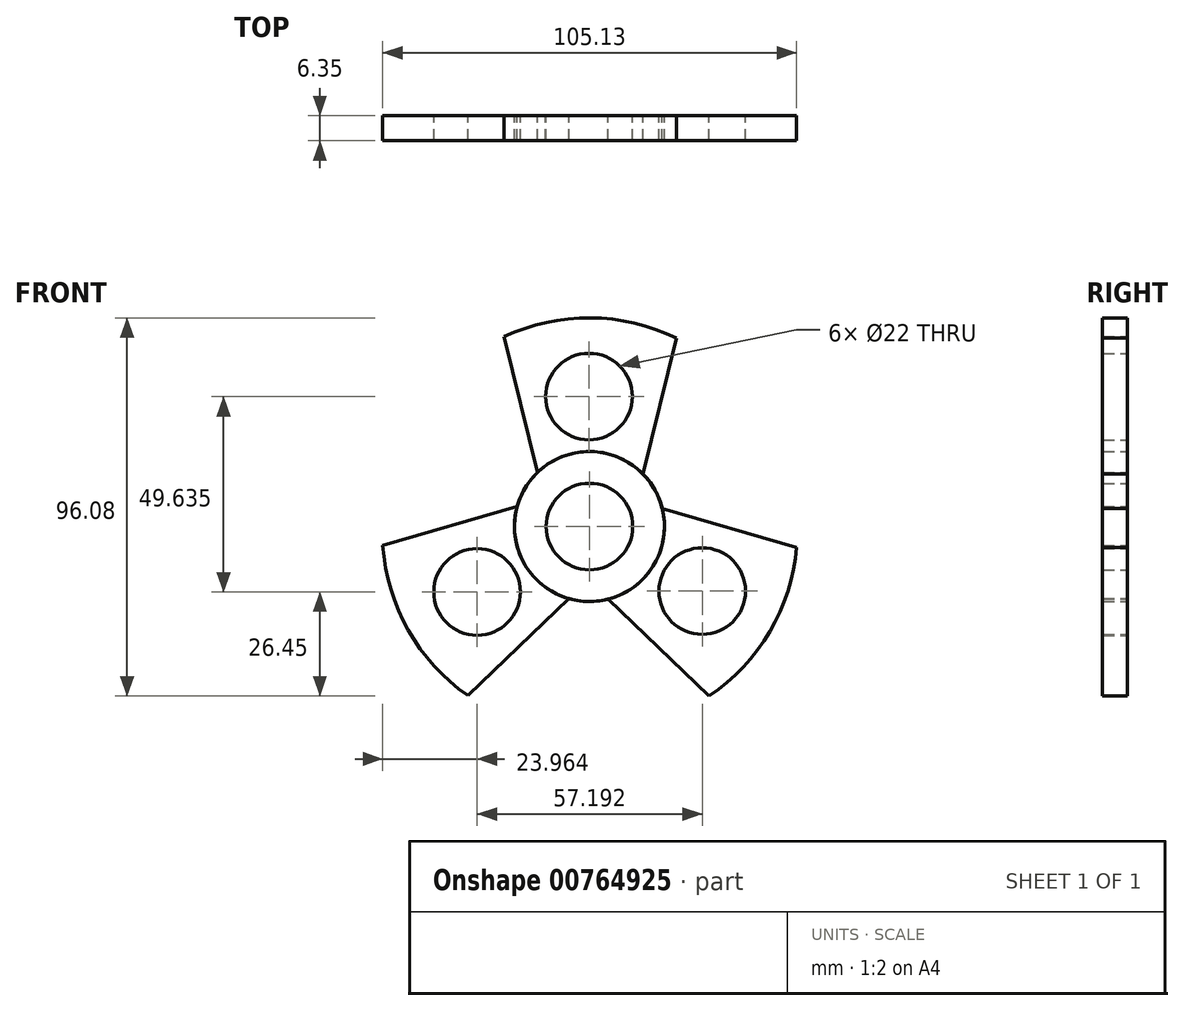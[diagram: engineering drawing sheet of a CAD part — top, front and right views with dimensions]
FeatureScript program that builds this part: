
annotation { "Feature Type Name" : "Feature", "Feature Type Description" : "" }
export const myFeature = defineFeature(function(context is Context, id is Id, definition is map)
    precondition{}
    {
        {
            var Q0;
            Q0=qCreatedBy(makeId("Front.planeOp"),FACE);
            var sketch = newSketch(context, id + "F0", { "sketchPlane" : qUnion([Q0])});
            skLineSegment(sketch, "E0", {"start": v(22.08, 42.03) * mm, "end": v(13.6, 7.5) * mm});
            skLineSegment(sketch, "E1", {"start": v(-21.72, 42.4) * mm, "end": v(-13.24, 7.86) * mm});
            skArc(sketch, "E2", {"start": v(22.08, 42.03) * mm, "mid": v(0.22, 47.18) * mm, "end": v(-21.72, 42.4) * mm});
            skCircle(sketch, "E3", {"center": v(-0.12, 27.18) * mm, "radius": 11 * mm});
            skCircle(sketch, "E4", {"center": v(0, -5.84) * mm, "radius": 19.05 * mm});
            skCircle(sketch, "E5", {"center": v(0, -5.84) * mm, "radius": 11 * mm});
            skSolve(sketch);
        }
        {
            var Q0;
            Q0 = qSketchRegion(id + "F0", true);
            extrude(context, id + "F1", {"entities" : qUnion([Q0]), "depth" : 6.35 * mm, "offsetDistance" : 25.4 * mm});
        }
        {
            var Q0;
            Q0=makeQuery(id+"F1.opExtrude","SWEPT_BODY",BODY,{"disambiguationData":[OSD([sQuery(id+"F0.wireOp",EDGE,"E0"),sQuery(id+"F0.wireOp",EDGE,"E1"),sQuery(id+"F0.wireOp",EDGE,"E2"),sQuery(id+"F0.wireOp",EDGE,"E3"),sQuery(id+"F0.wireOp",EDGE,"E4"),sQuery(id+"F0.wireOp",EDGE,"E5"),sQuery(id+"F0.wireOp",EDGE,"skdJ2RkB-3yUG-p0Ua-GYZb-yKCTIOwcBmh8"),sQuery(id+"F0.wireOp",EDGE,"e9sZvFhc-D5Zj-pzDT-xpeE-XVcC86HEpHMD")])]});
            var Q1;
            Q1=sQuery(id+"F0.wireOp",EDGE,"E5");
            circularPattern(context, id + "F2", {"entities" : qUnion([Q0]), "axis" : qUnion([Q1]), "angle" : 360 * degree, "instanceCount" : 3, "equalSpace" : true});
        }
    });
